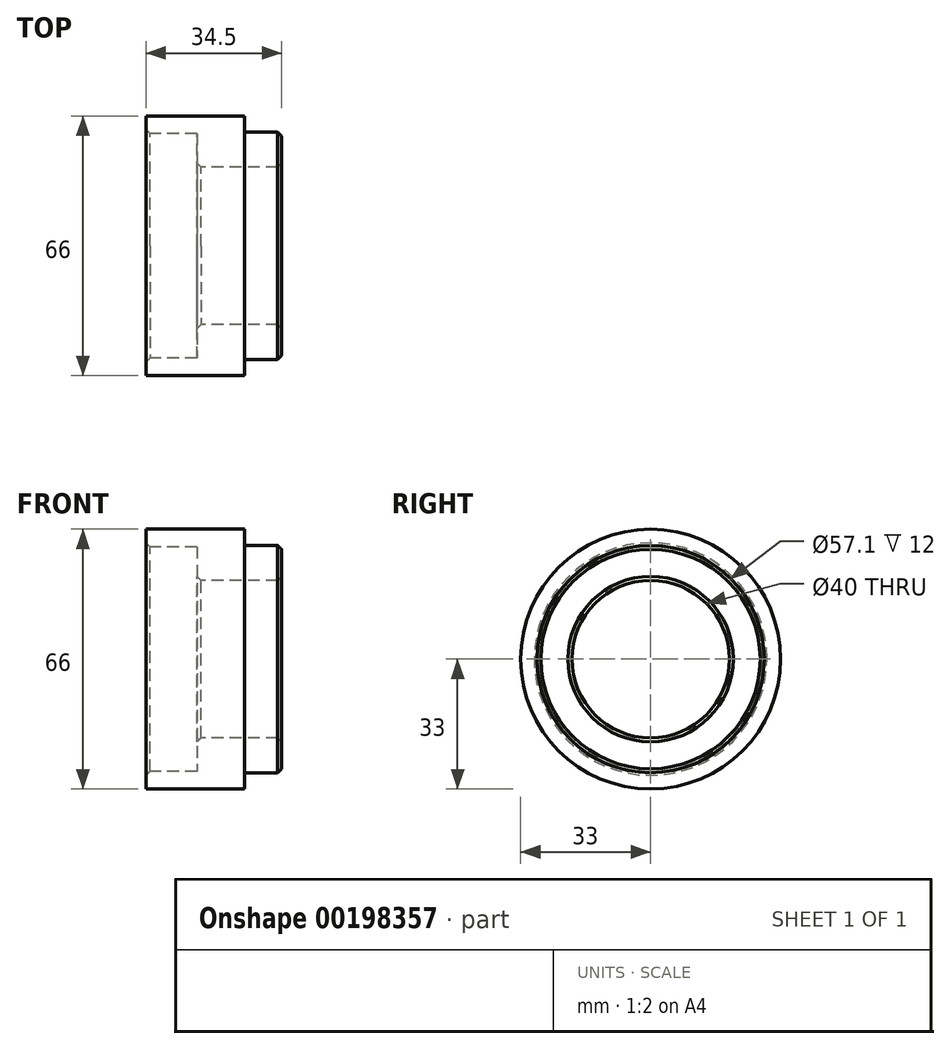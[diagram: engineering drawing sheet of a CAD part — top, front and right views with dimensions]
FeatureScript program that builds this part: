
annotation { "Feature Type Name" : "Feature", "Feature Type Description" : "" }
export const myFeature = defineFeature(function(context is Context, id is Id, definition is map)
    precondition{}
    {
        {
            var Q0;
            Q0=qCreatedBy(makeId("Front.planeOp"),FACE);
            var sketch = newSketch(context, id + "F0", { "sketchPlane" : qUnion([Q0])});
            skLineSegment(sketch, "E0", {"start": v(-159.38, 0) * mm, "end": v(166.26, 0) * mm, "construction": true});
            skLineSegment(sketch, "E1", {"start": v(0, -95.28) * mm, "end": v(0, 96.66) * mm, "construction": true});
            skLineSegment(sketch, "E2.bottom", {"start": v(0, 33) * mm, "end": v(25, 33) * mm});
            skLineSegment(sketch, "E2.top", {"start": v(0, 28.55) * mm, "end": v(13, 28.55) * mm});
            skLineSegment(sketch, "E2.left", {"start": v(0, 33) * mm, "end": v(0, 28.55) * mm});
            skLineSegment(sketch, "E3.top", {"start": v(13, 20) * mm, "end": v(34.5, 20) * mm});
            skLineSegment(sketch, "E3.left", {"start": v(13, 28.55) * mm, "end": v(13, 20) * mm});
            skLineSegment(sketch, "E4", {"start": v(34.5, 20) * mm, "end": v(34.5, 28.86) * mm});
            skLineSegment(sketch, "E5.top", {"start": v(25, 28.86) * mm, "end": v(34.5, 28.86) * mm});
            skLineSegment(sketch, "E5.left", {"start": v(25, 33) * mm, "end": v(25, 28.86) * mm});
            skSolve(sketch);
        }
        {
            var Q0;
            Q0=qSketchRegion(id+"F0",true);
            var Q1;
            Q1=sQuery(id+"F0.wireOp",EDGE,"E0");
            revolve(context, id + "F1", {"entities" : qUnion([Q0]), "axis" : qUnion([Q1]), "revolveType" : RevolveType.FULL});
        }
        {
            var Q0;
            Q0=makeQuery(id+"F1.opRevolve","SWEPT_EDGE",EDGE,{"disambiguationData":[OSD([sQuery(id+"F0.wireOp",EDGE,"E2.top"),sQuery(id+"F0.wireOp",EDGE,"E2.left")])]});
            var Q1;
            Q1=makeQuery(id+"F1.opRevolve","SWEPT_EDGE",EDGE,{"disambiguationData":[OSD([sQuery(id+"F0.wireOp",EDGE,"E3.top"),sQuery(id+"F0.wireOp",EDGE,"E4")])]});
            var Q2;
            Q2=makeQuery(id+"F1.opRevolve","SWEPT_FACE",FACE,{"disambiguationData":[OSD([sQuery(id+"F0.wireOp",EDGE,"E4")])]});
            var Q3;
            Q3=makeQuery(id+"F1.opRevolve","SWEPT_EDGE",EDGE,{"disambiguationData":[OSD([sQuery(id+"F0.wireOp",EDGE,"E3.top"),sQuery(id+"F0.wireOp",EDGE,"E3.left")])]});
            chamfer(context, id + "F2", {"entities" : qUnion([Q0, Q1, Q2, Q3]), "width" : 1 * mm, "tangentPropagation" : true});
        }
    });
